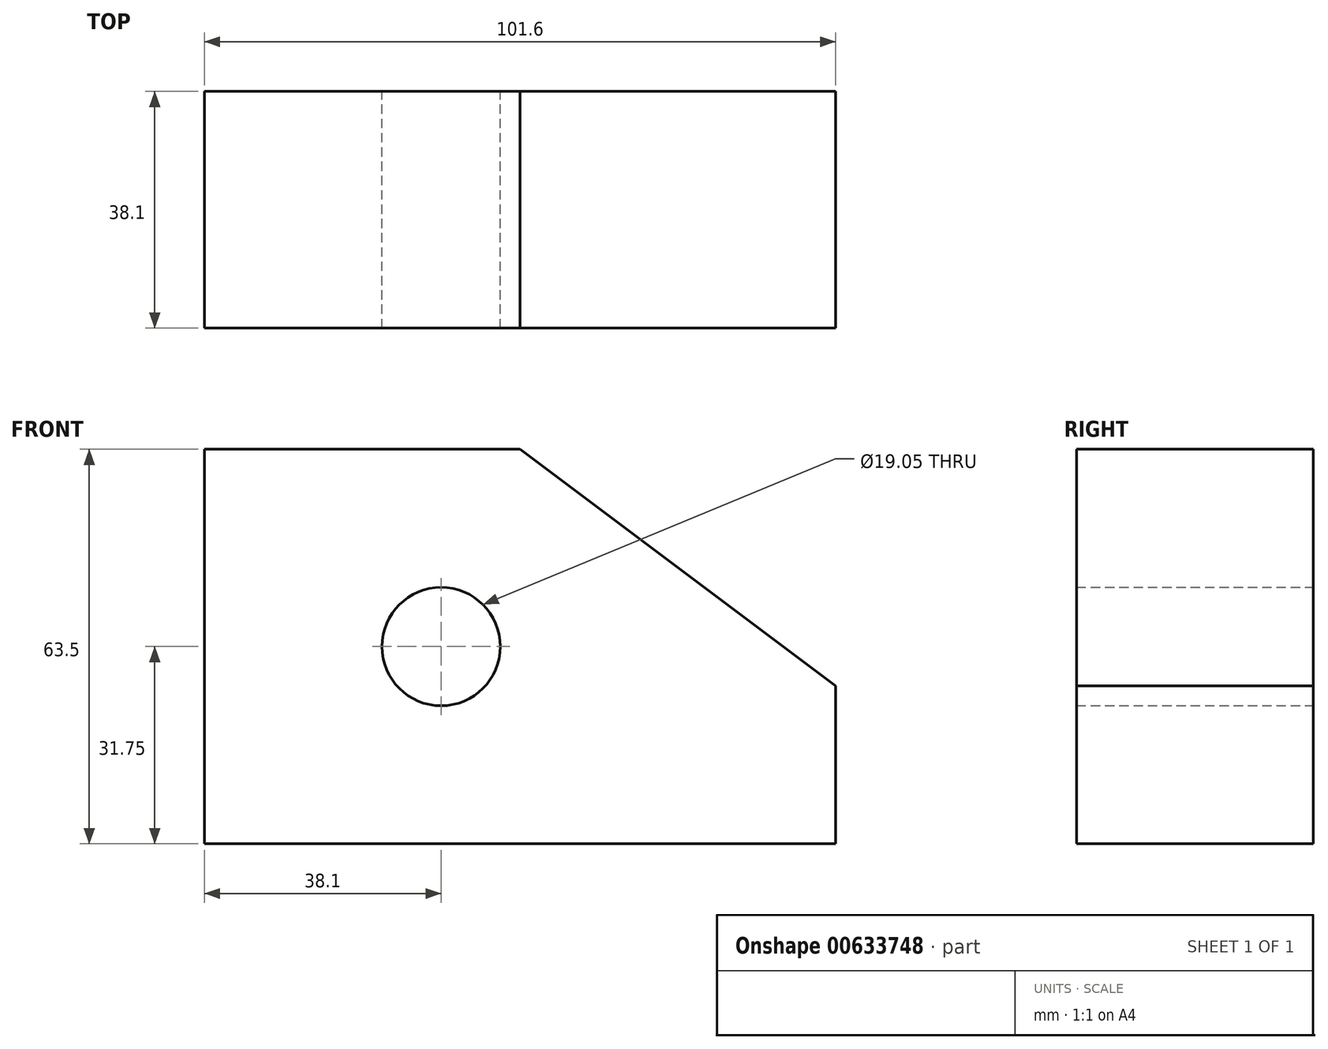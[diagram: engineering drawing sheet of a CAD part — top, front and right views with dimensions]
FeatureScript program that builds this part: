
annotation { "Feature Type Name" : "Feature", "Feature Type Description" : "" }
export const myFeature = defineFeature(function(context is Context, id is Id, definition is map)
    precondition{}
    {
        {
            var Q0;
            Q0=qCreatedBy(makeId("Front.planeOp"),FACE);
            var sketch = newSketch(context, id + "F0", { "sketchPlane" : qUnion([Q0])});
            skLineSegment(sketch, "E0", {"start": v(0, 0) * mm, "end": v(0, 63.5) * mm});
            skLineSegment(sketch, "E1", {"start": v(0, 63.5) * mm, "end": v(50.8, 63.5) * mm});
            skLineSegment(sketch, "E2", {"start": v(50.8, 63.5) * mm, "end": v(101.6, 25.4) * mm});
            skLineSegment(sketch, "E3", {"start": v(101.6, 25.4) * mm, "end": v(101.6, 0) * mm});
            skLineSegment(sketch, "E4", {"start": v(101.6, 0) * mm, "end": v(0, 0) * mm});
            skCircle(sketch, "E5", {"center": v(38.1, 31.75) * mm, "radius": 9.53 * mm});
            skSolve(sketch);
        }
        {
            var Q0;
            Q0=makeQuery(id+"F0.imprint","IMPRINT",FACE,{"disambiguationData":[TD([[makeQuery(id+"F0.imprint","IMPRINT",EDGE,{"derivedFrom":sQuery(id+"F0.wireOp",EDGE,"E0")}),-1.0]])]});
            extrude(context, id + "F1", {"entities" : qUnion([Q0]), "depth" : 38.1 * mm, "offsetDistance" : 25.4 * mm});
        }
    });
